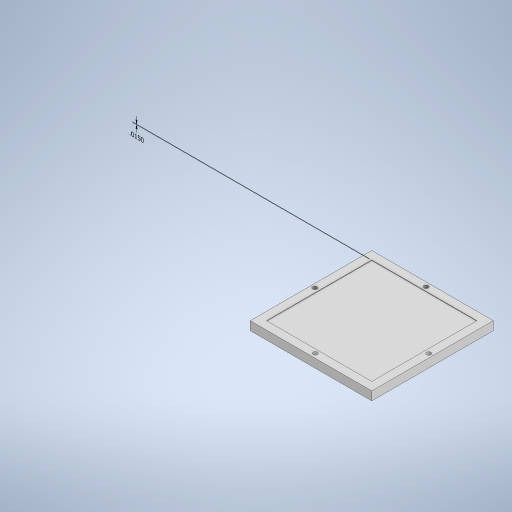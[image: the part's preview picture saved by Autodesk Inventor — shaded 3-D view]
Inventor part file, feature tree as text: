
AUTODESK INVENTOR PART (.ipt)
format: ipt  version: 2024.2 (Build 282272000, 272)  size: 262,656 bytes
history: native  units: in
note: dims shown in document units (in); Inventor stores cm internally (conversion verified against a paired STEP export)
features: other x2, extrude x2, sketch x2, shell x1
ambient origin geometry x8: Origin, YZ Plane, XZ Plane, XY Plane, X Axis, Y Axis, Z Axis, Center Point
bodies: Solid1 (feature_tree)
feature tree (7):
  other  "Annotations"
  extrude  "Extrusion1"  Depth=3.5in
  shell  "Shell1"  Thickness=0.25in
  extrude  "Extrusion2"  Depth=0.125in
  sketch  "Sketch1"  dims[d0=3.5in d1=3.5in d2=0.25in d3=0.0in]
  sketch  "Sketch2"  dims[d4=0.235in d8=0.125in d10=0.1125in d11=0.125in d12=0.1125in d13=1.75in d14=0.125in d15=0.1125in d16=0.125in d17=0.1125in d18=0.125in d19=0.0in d5=0.0in d6=0.3937in d7=0.015in]
  other  "Linear Dimension 1"
